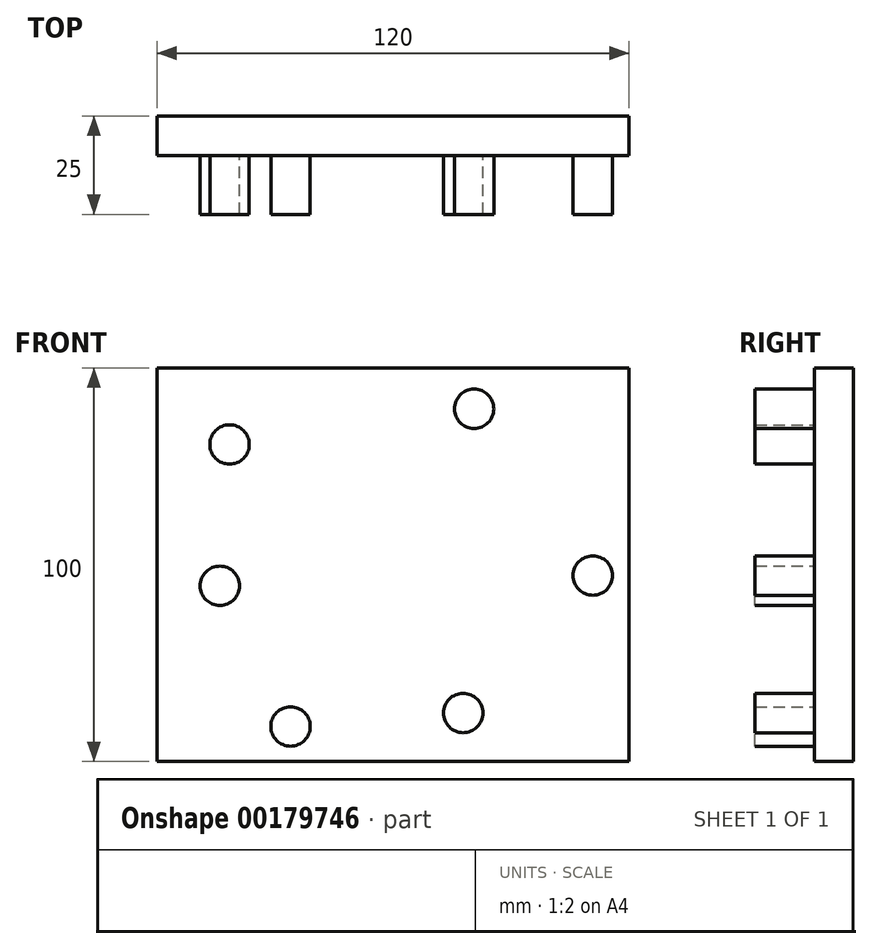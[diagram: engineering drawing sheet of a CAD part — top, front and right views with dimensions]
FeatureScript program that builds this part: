
annotation { "Feature Type Name" : "Feature", "Feature Type Description" : "" }
export const myFeature = defineFeature(function(context is Context, id is Id, definition is map)
    precondition{}
    {
        {
            var Q0;
            Q0=qCreatedBy(makeId("Front.planeOp"),FACE);
            var sketch = newSketch(context, id + "F0", { "sketchPlane" : qUnion([Q0])});
            skLineSegment(sketch, "E0.bottom", {"start": v(60, 50) * mm, "end": v(-60, 50) * mm});
            skLineSegment(sketch, "E0.top", {"start": v(60, -50) * mm, "end": v(-60, -50) * mm});
            skLineSegment(sketch, "E0.left", {"start": v(60, 50) * mm, "end": v(60, -50) * mm});
            skLineSegment(sketch, "E0.right", {"start": v(-60, 50) * mm, "end": v(-60, -50) * mm});
            skPoint(sketch, "E0.middle", {"position": v(0, 0) * mm});
            skSolve(sketch);
        }
        {
            var Q0;
            Q0=makeQuery(id+"F0.imprint","IMPRINT",FACE,{"disambiguationData":[TD([[makeQuery(id+"F0.imprint","IMPRINT",EDGE,{"derivedFrom":sQuery(id+"F0.wireOp",EDGE,"E0.bottom")}),1.0]])]});
            extrude(context, id + "F1", {"entities" : qUnion([Q0]), "depth" : 10 * mm});
        }
        {
            var Q0;
            Q0=makeQuery(id+"F1.opExtrude","CAP_FACE",FACE,{"disambiguationData":[OSD([sQuery(id+"F0.wireOp",EDGE,"E0.bottom"),sQuery(id+"F0.wireOp",EDGE,"E0.top"),sQuery(id+"F0.wireOp",EDGE,"E0.left"),sQuery(id+"F0.wireOp",EDGE,"E0.right")])],"isStart":false});
            var sketch = newSketch(context, id + "F2", { "sketchPlane" : qUnion([Q0])});
            skCircle(sketch, "E1", {"center": v(-41.52, 30.55) * mm, "radius": 5 * mm});
            skCircle(sketch, "E2", {"center": v(-43.99, -5.36) * mm, "radius": 5 * mm});
            skCircle(sketch, "E3", {"center": v(-26.03, -41.1) * mm, "radius": 5 * mm});
            skCircle(sketch, "E4", {"center": v(17.83, -37.68) * mm, "radius": 5 * mm});
            skCircle(sketch, "E5", {"center": v(50.76, -2.75) * mm, "radius": 5 * mm});
            skCircle(sketch, "E6", {"center": v(20.6, 39.6) * mm, "radius": 5 * mm});
            skSolve(sketch);
        }
        {
            var Q0;
            Q0 = qSketchRegion(id + "F2", true);
            extrude(context, id + "F3", {"entities" : qUnion([Q0]), "operationType" : NewBodyOperationType.ADD, "depth" : 15 * mm});
        }
    });
